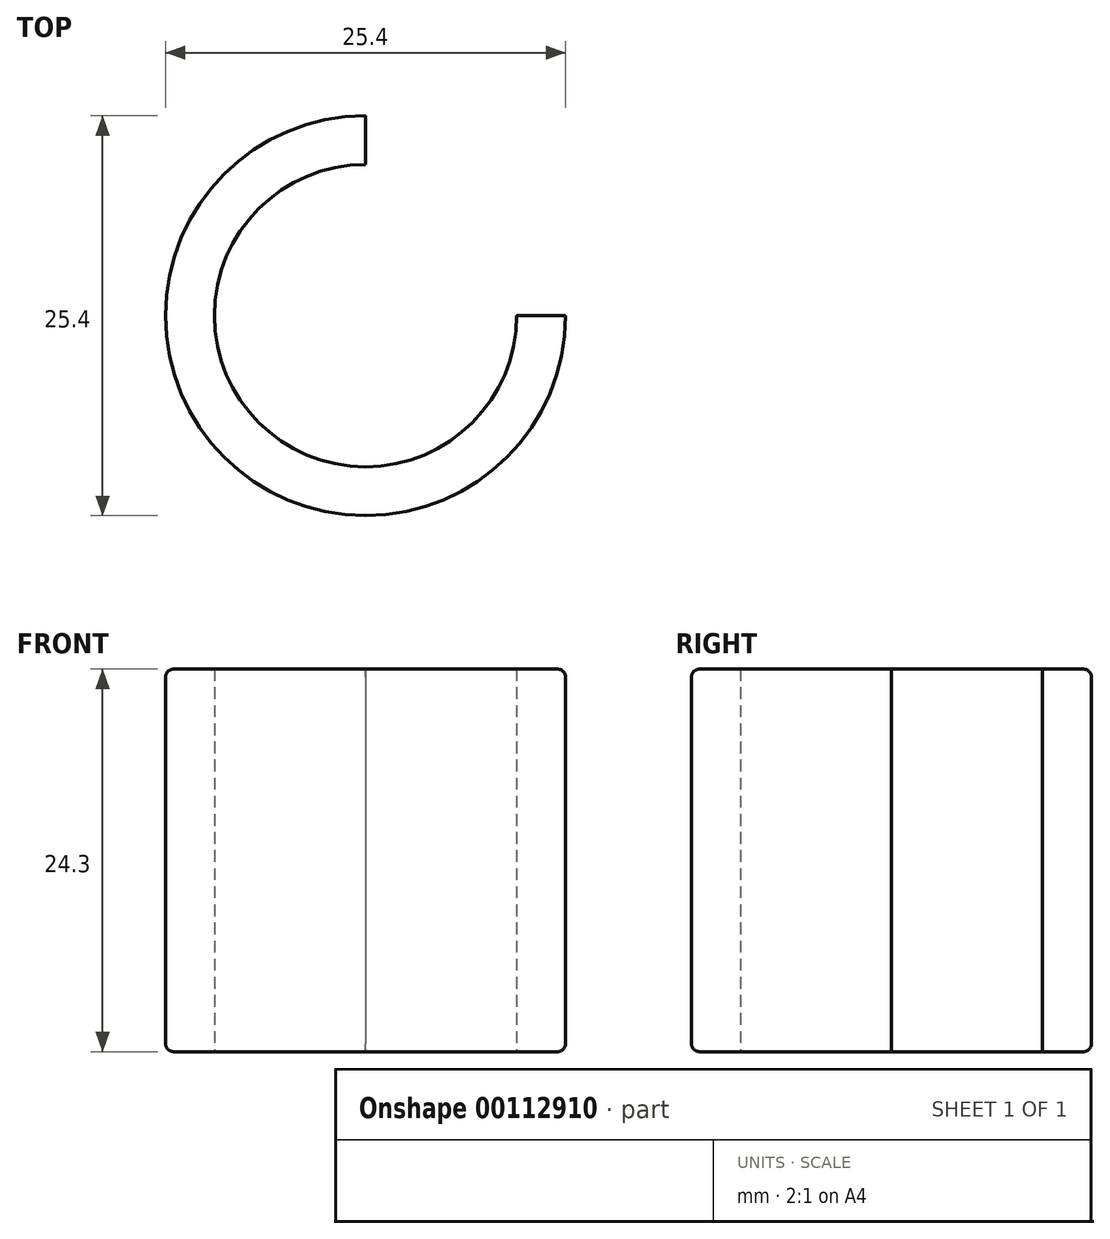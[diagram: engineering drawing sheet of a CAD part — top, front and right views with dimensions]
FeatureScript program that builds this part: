
annotation { "Feature Type Name" : "Feature", "Feature Type Description" : "" }
export const myFeature = defineFeature(function(context is Context, id is Id, definition is map)
    precondition{}
    {
        {
            var Q0;
            Q0=qCreatedBy(makeId("Top.planeOp"),FACE);
            var sketch = newSketch(context, id + "F0", { "sketchPlane" : qUnion([Q0])});
            skCircle(sketch, "E0", {"center": v(0, 0) * mm, "radius": 12.7 * mm});
            skCircle(sketch, "E1", {"center": v(0, 0) * mm, "radius": 9.6 * mm});
            skSolve(sketch);
        }
        {
            var Q0;
            Q0 = qSketchRegion(id + "F0", true);
            extrude(context, id + "F1", {"entities" : qUnion([Q0]), "depth" : 16.5 * mm});
        }
        {
            var Q0;
            Q0=makeQuery(id+"F1.opExtrude","CAP_FACE",FACE,{"disambiguationData":[OSD([sQuery(id+"F0.wireOp",EDGE,"E0"),sQuery(id+"F0.wireOp",EDGE,"E1")])],"isStart":false});
            var sketch = newSketch(context, id + "F2", { "sketchPlane" : qUnion([Q0])});
            skLineSegment(sketch, "E2.bottom", {"start": v(0, 0) * mm, "end": v(14.32, 0) * mm});
            skLineSegment(sketch, "E2.top", {"start": v(0, 14.05) * mm, "end": v(14.32, 14.05) * mm});
            skLineSegment(sketch, "E2.left", {"start": v(0, 0) * mm, "end": v(0, 14.05) * mm});
            skLineSegment(sketch, "E2.right", {"start": v(14.32, 0) * mm, "end": v(14.32, 14.05) * mm});
            skSolve(sketch);
        }
        {
            var Q0;
            Q0 = qSketchRegion(id + "F2", true);
            extrude(context, id + "F3", {"entities" : qUnion([Q0]), "operationType" : NewBodyOperationType.REMOVE, "endBound" : BoundingType.THROUGH_ALL, "oppositeDirection" : true, "depth" : 25 * mm});
        }
        {
            var Q0;
            Q0=makeQuery(id+"F1.opExtrude","CAP_FACE",FACE,{"disambiguationData":[OSD([sQuery(id+"F0.wireOp",EDGE,"E0"),sQuery(id+"F0.wireOp",EDGE,"E1")])],"isStart":false});
            extrude(context, id + "F4", {"entities" : qUnion([Q0]), "operationType" : NewBodyOperationType.ADD, "depth" : 7.8 * mm});
        }
        {
            var Q0;
            Q0=makeQuery(id+"F4.opExtrude","CAP_EDGE",EDGE,{"disambiguationData":[OSD([sQuery(id+"F0.wireOp",EDGE,"E0")])],"isStart":false});
            var Q1;
            Q1=makeQuery(id+"F1.opExtrude","CAP_EDGE",EDGE,{"disambiguationData":[OSD([sQuery(id+"F0.wireOp",EDGE,"E0")])],"isStart":true});
            fillet(context, id + "F5", {"entities" : qUnion([Q0, Q1]), "radius" : .5 * mm, "tangentPropagation" : true, "allowEdgeOverflow" : false});
        }
    });
